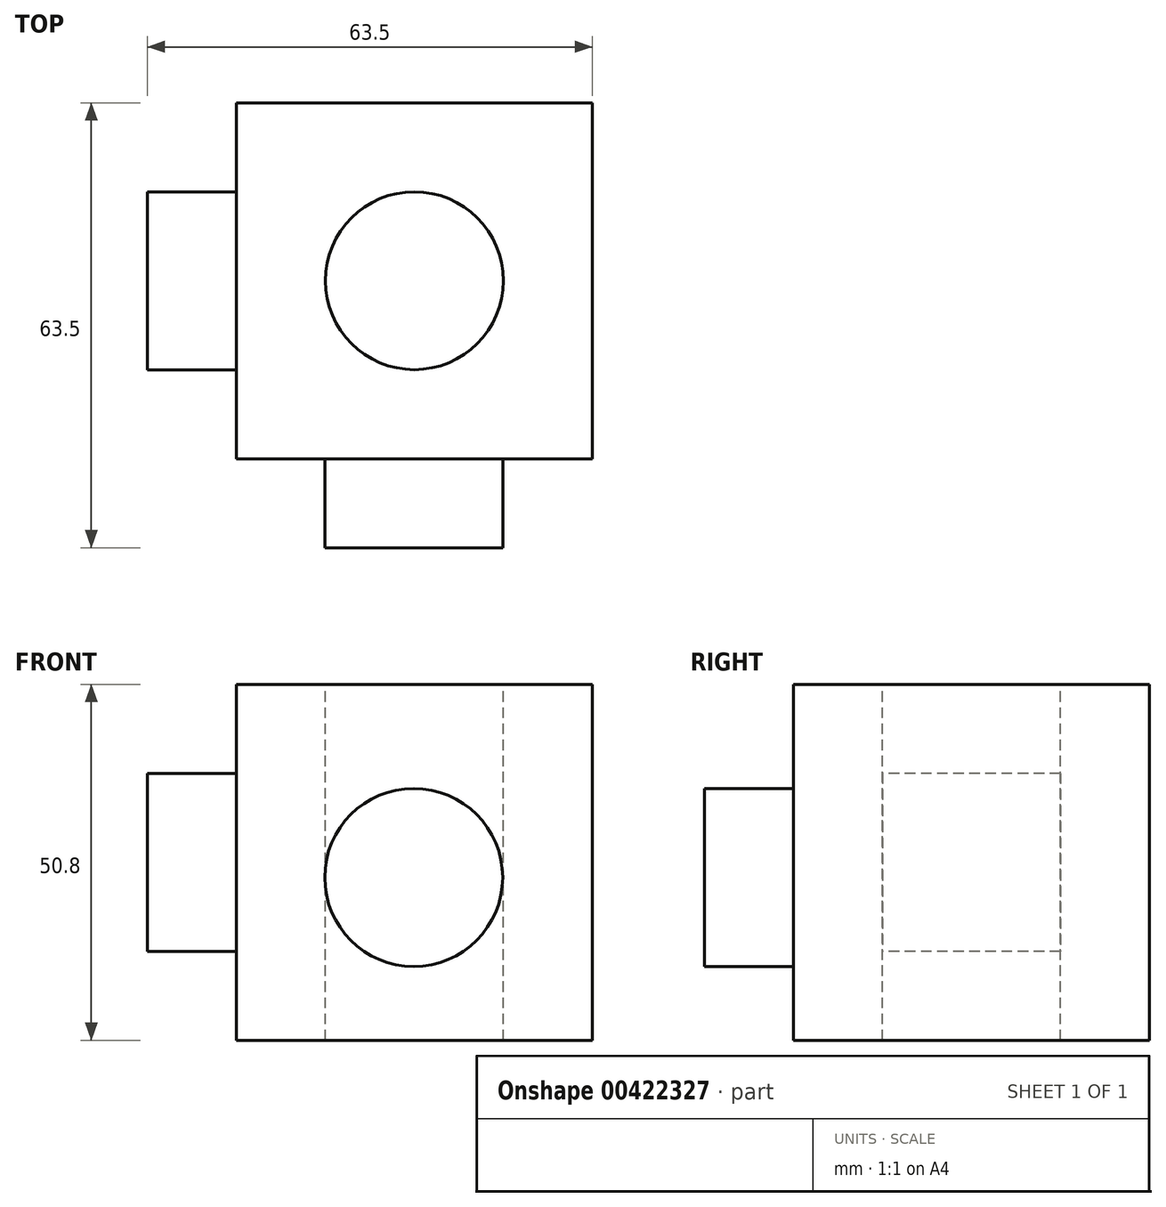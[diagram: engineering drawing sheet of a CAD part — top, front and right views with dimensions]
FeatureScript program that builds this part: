
annotation { "Feature Type Name" : "Feature", "Feature Type Description" : "" }
export const myFeature = defineFeature(function(context is Context, id is Id, definition is map)
    precondition{}
    {
        {
            var Q0;
            Q0=qCreatedBy(makeId("Front.planeOp"),FACE);
            var sketch = newSketch(context, id + "F0", { "sketchPlane" : qUnion([Q0])});
            skLineSegment(sketch, "E0", {"start": v(0, 0) * mm, "end": v(0, 50.8) * mm});
            skLineSegment(sketch, "E1", {"start": v(0, 0) * mm, "end": v(-50.8, 0) * mm});
            skLineSegment(sketch, "E2", {"start": v(0, 50.8) * mm, "end": v(-50.8, 50.8) * mm});
            skLineSegment(sketch, "E3", {"start": v(-50.8, 50.8) * mm, "end": v(-50.8, 0) * mm});
            skSolve(sketch);
        }
        {
            var Q0;
            Q0=makeQuery(id+"F0.imprint","IMPRINT",FACE,{"disambiguationData":[TD([[makeQuery(id+"F0.imprint","IMPRINT",EDGE,{"derivedFrom":sQuery(id+"F0.wireOp",EDGE,"E0")}),1.0]])]});
            extrude(context, id + "F1", {"entities" : qUnion([Q0]), "depth" : 50.8 * mm});
        }
        {
            var Q0;
            Q0=makeQuery(id+"F1.opExtrude","CAP_FACE",FACE,{"disambiguationData":[OSD([sQuery(id+"F0.wireOp",EDGE,"E0"),sQuery(id+"F0.wireOp",EDGE,"E1"),sQuery(id+"F0.wireOp",EDGE,"E2"),sQuery(id+"F0.wireOp",EDGE,"E3")])],"isStart":false});
            var sketch = newSketch(context, id + "F2", { "sketchPlane" : qUnion([Q0])});
            skCircle(sketch, "E4", {"center": v(-25.5, 23.24) * mm, "radius": 12.7 * mm});
            skSolve(sketch);
        }
        {
            var Q0;
            Q0=makeQuery(id+"F2.imprint","IMPRINT",FACE,{"disambiguationData":[TD([[makeQuery(id+"F2.imprint","IMPRINT",EDGE,{"derivedFrom":sQuery(id+"F2.wireOp",EDGE,"E4")}),1.0]])]});
            var sketch = newSketch(context, id + "F3", { "sketchPlane" : qUnion([Q0])});
            skSolve(sketch);
        }
        {
            var Q0;
            Q0=makeQuery(id+"F2.imprint","IMPRINT",FACE,{"disambiguationData":[TD([[makeQuery(id+"F2.imprint","IMPRINT",EDGE,{"derivedFrom":sQuery(id+"F2.wireOp",EDGE,"E4")}),1.0]])]});
            extrude(context, id + "F4", {"entities" : qUnion([Q0]), "operationType" : NewBodyOperationType.ADD, "depth" : -50.8 * mm});
        }
        {
            var Q0;
            Q0=makeQuery(id+"F3.imprint","IMPRINT",FACE,{"disambiguationData":[TD([[makeQuery(id+"F3.imprint","IMPRINT",EDGE,{"derivedFrom":makeQuery(id+"F2.imprint","IMPRINT",EDGE,{"derivedFrom":sQuery(id+"F2.wireOp",EDGE,"E4")})}),1.0]])]});
            extrude(context, id + "F5", {"entities" : qUnion([Q0]), "operationType" : NewBodyOperationType.ADD, "depth" : 12.7 * mm});
        }
        {
            var Q0;
            Q0=makeQuery(id+"F1.opExtrude","SWEPT_FACE",FACE,{"disambiguationData":[OSD([sQuery(id+"F0.wireOp",EDGE,"E2")])]});
            var sketch = newSketch(context, id + "F6", { "sketchPlane" : qUnion([Q0])});
            skCircle(sketch, "E5", {"center": v(-25.4, -25.4) * mm, "radius": 12.7 * mm});
            skSolve(sketch);
        }
        {
            var Q0;
            Q0 = qSketchRegion(id + "F6", true);
            extrude(context, id + "F7", {"entities" : qUnion([Q0]), "operationType" : NewBodyOperationType.REMOVE, "oppositeDirection" : true, "depth" : 50.8 * mm});
        }
        {
            var Q0;
            Q0=makeQuery(id+"F1.opExtrude","SWEPT_FACE",FACE,{"disambiguationData":[OSD([sQuery(id+"F0.wireOp",EDGE,"E3")])]});
            var sketch = newSketch(context, id + "F8", { "sketchPlane" : qUnion([Q0])});
            skLineSegment(sketch, "E6.bottom", {"start": v(12.7, 38.1) * mm, "end": v(38.1, 38.1) * mm});
            skLineSegment(sketch, "E6.top", {"start": v(12.7, 12.7) * mm, "end": v(38.1, 12.7) * mm});
            skLineSegment(sketch, "E6.left", {"start": v(12.7, 38.1) * mm, "end": v(12.7, 12.7) * mm});
            skLineSegment(sketch, "E6.right", {"start": v(38.1, 38.1) * mm, "end": v(38.1, 12.7) * mm});
            skSolve(sketch);
        }
        {
            var Q0;
            Q0 = qSketchRegion(id + "F8", true);
            extrude(context, id + "F9", {"entities" : qUnion([Q0]), "operationType" : NewBodyOperationType.ADD, "depth" : 12.7 * mm});
        }
    });
